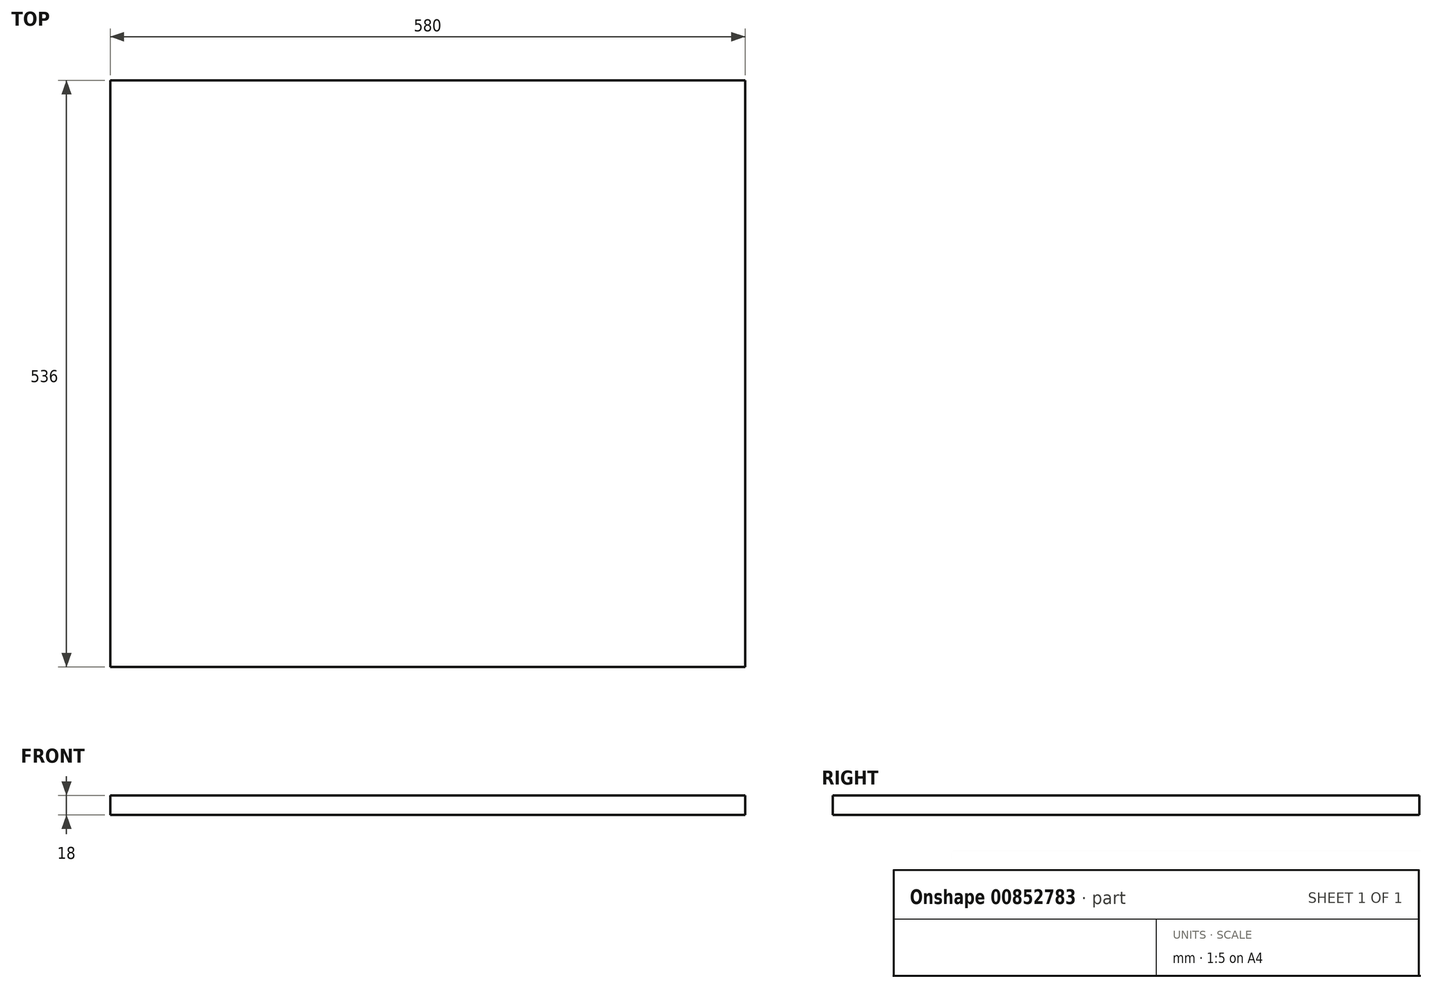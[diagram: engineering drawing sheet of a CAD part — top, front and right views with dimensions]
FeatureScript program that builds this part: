
annotation { "Feature Type Name" : "Feature", "Feature Type Description" : "" }
export const myFeature = defineFeature(function(context is Context, id is Id, definition is map)
    precondition{}
    {
        {
            var Q0;
            Q0=qCreatedBy(makeId("Top.planeOp"),FACE);
            var sketch = newSketch(context, id + "F0", { "sketchPlane" : qUnion([Q0])});
            skLineSegment(sketch, "E0.bottom", {"start": v(290, -268) * mm, "end": v(-290, -268) * mm});
            skLineSegment(sketch, "E0.top", {"start": v(290, 268) * mm, "end": v(-290, 268) * mm});
            skLineSegment(sketch, "E0.left", {"start": v(290, -268) * mm, "end": v(290, 268) * mm});
            skLineSegment(sketch, "E0.right", {"start": v(-290, -268) * mm, "end": v(-290, 268) * mm});
            skPoint(sketch, "E0.middle", {"position": v(0, 0) * mm});
            skSolve(sketch);
        }
        {
            var Q0;
            Q0 = qSketchRegion(id + "F0", true);
            extrude(context, id + "F1", {"entities" : qUnion([Q0]), "depth" : 18 * mm, "offsetDistance" : 25 * mm});
        }
    });
